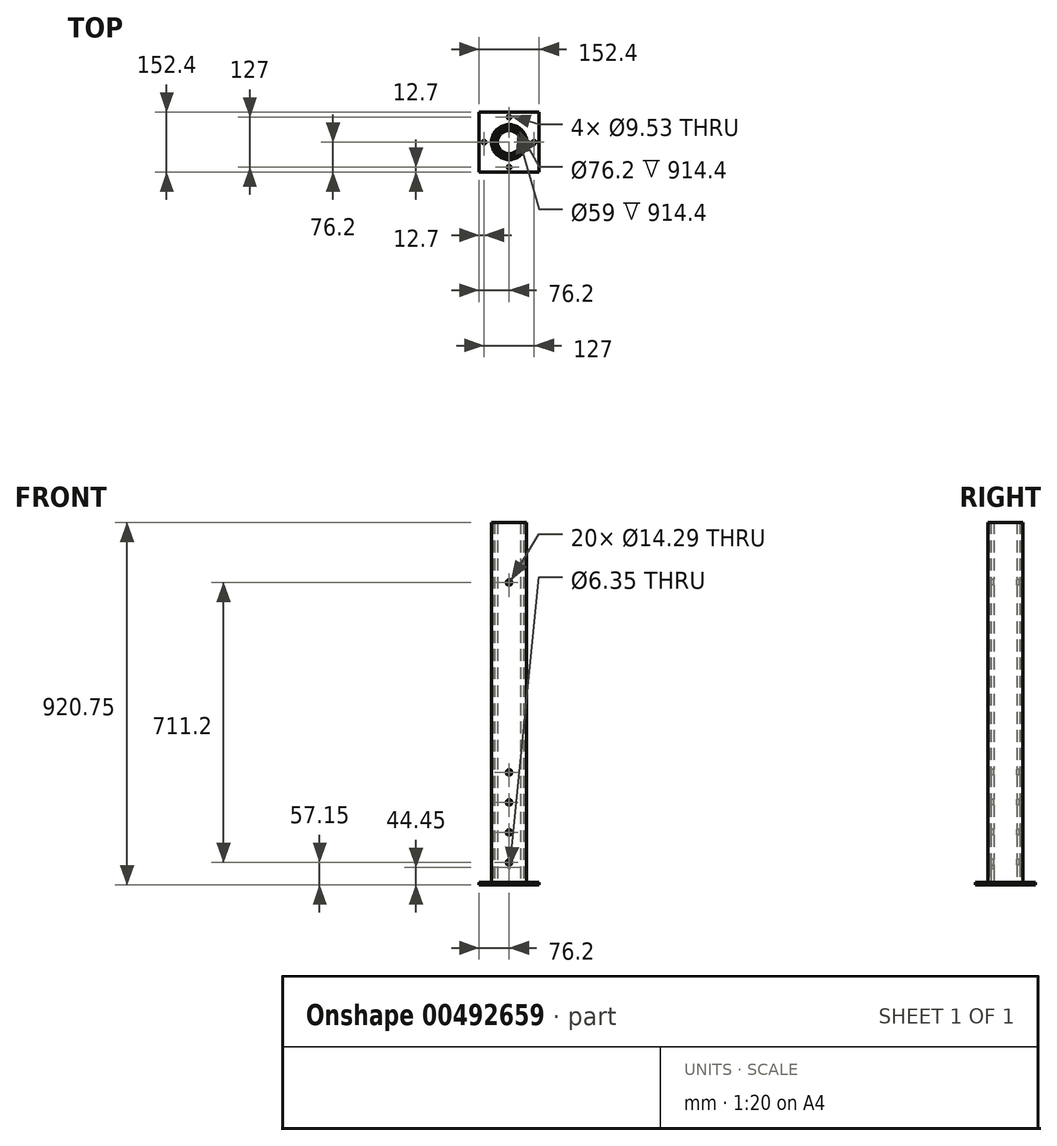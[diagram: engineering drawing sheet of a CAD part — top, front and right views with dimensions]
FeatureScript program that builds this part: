
annotation { "Feature Type Name" : "Feature", "Feature Type Description" : "" }
export const myFeature = defineFeature(function(context is Context, id is Id, definition is map)
    precondition{}
    {
        {
            var Q0;
            Q0=qCreatedBy(makeId("Top.planeOp"),FACE);
            var sketch = newSketch(context, id + "F0", { "sketchPlane" : qUnion([Q0])});
            skCircle(sketch, "E0", {"center": v(0, 0) * mm, "radius": 44.45 * mm});
            skCircle(sketch, "E1", {"center": v(0, 0) * mm, "radius": 38.1 * mm});
            skSolve(sketch);
        }
        {
            var Q0;
            Q0 = qSketchRegion(id + "F0", true);
            extrude(context, id + "F1", {"entities" : qUnion([Q0]), "depth" : 76.2 * mm, "offsetDistance" : 25 * mm});
        }
        {
            var Q0;
            Q0 = qSketchRegion(id + "F0", true);
            extrude(context, id + "F2", {"entities" : qUnion([Q0]), "depth" : 25.4 * mm, "offsetDistance" : 25 * mm});
        }
        {
            var Q0;
            Q0=qCreatedBy(makeId("Top.planeOp"),FACE);
            var sketch = newSketch(context, id + "F3", { "sketchPlane" : qUnion([Q0])});
            skCircle(sketch, "E2", {"center": v(0, 0) * mm, "radius": 36.51 * mm});
            skCircle(sketch, "E3", {"center": v(0, 0) * mm, "radius": 29.5 * mm});
            skSolve(sketch);
        }
        {
            var Q0;
            Q0 = qSketchRegion(id + "F3", true);
            extrude(context, id + "F4", {"entities" : qUnion([Q0]), "depth" : 914.4 * mm, "offsetDistance" : 25 * mm});
        }
        {
            var Q0;
            Q0=qCreatedBy(makeId("Front.planeOp"),FACE);
            var sketch = newSketch(context, id + "F5", { "sketchPlane" : qUnion([Q0])});
            skCircle(sketch, "E4", {"center": v(0, 38.1) * mm, "radius": 3.18 * mm});
            skSolve(sketch);
        }
        {
            var Q0;
            Q0 = qSketchRegion(id + "F5", true);
            extrude(context, id + "F6", {"entities" : qUnion([Q0]), "operationType" : NewBodyOperationType.REMOVE, "depth" : 50.8 * mm, "offsetDistance" : 25 * mm});
        }
        {
            var Q0;
            Q0=qCreatedBy(makeId("Top.planeOp"),FACE);
            var sketch = newSketch(context, id + "F7", { "sketchPlane" : qUnion([Q0])});
            skCircle(sketch, "E5", {"center": v(0, 0) * mm, "radius": 44.45 * mm});
            skCircle(sketch, "E6", {"center": v(0, 0) * mm, "radius": 38.1 * mm});
            skSolve(sketch);
        }
        {
            var Q0;
            Q0 = qSketchRegion(id + "F7", true);
            extrude(context, id + "F8", {"entities" : qUnion([Q0]), "depth" : 914.4 * mm, "offsetDistance" : 25 * mm});
        }
        {
            var Q0;
            Q0=qCreatedBy(makeId("Front.planeOp"),FACE);
            var sketch = newSketch(context, id + "F9", { "sketchPlane" : qUnion([Q0])});
            skCircle(sketch, "E7", {"center": v(0, 50.8) * mm, "radius": 7.14 * mm});
            skCircle(sketch, "E8.0.1.0", {"center": v(0, 127) * mm, "radius": 7.14 * mm});
            skCircle(sketch, "E8.0.2.0", {"center": v(0, 203.2) * mm, "radius": 7.14 * mm});
            skCircle(sketch, "E8.0.3.0", {"center": v(0, 279.4) * mm, "radius": 7.14 * mm});
            skLineSegment(sketch, "E8.direction1", {"start": v(0, 50.8) * mm, "end": v(25, 50.8) * mm, "construction": true});
            skLineSegment(sketch, "E8.direction2", {"start": v(0, 50.8) * mm, "end": v(0, 127) * mm, "construction": true});
            skSolve(sketch);
        }
        {
            var Q0;
            Q0 = qSketchRegion(id + "F9", true);
            extrude(context, id + "F10", {"entities" : qUnion([Q0]), "operationType" : NewBodyOperationType.REMOVE, "endBound" : BoundingType.THROUGH_ALL, "oppositeDirection" : true, "depth" : 25 * mm, "offsetDistance" : 25 * mm, "hasSecondDirection" : true, "secondDirectionBound" : BoundingType.THROUGH_ALL, "secondDirectionOppositeDirection" : false, "secondDirectionDepth" : 25 * mm});
        }
        {
            var Q0;
            Q0=qCreatedBy(makeId("Front.planeOp"),FACE);
            var sketch = newSketch(context, id + "F11", { "sketchPlane" : qUnion([Q0])});
            skCircle(sketch, "E9", {"center": v(0, 762) * mm, "radius": 7.14 * mm});
            skSolve(sketch);
        }
        {
            var Q0;
            Q0 = qSketchRegion(id + "F11", true);
            extrude(context, id + "F12", {"entities" : qUnion([Q0]), "operationType" : NewBodyOperationType.REMOVE, "endBound" : BoundingType.THROUGH_ALL, "oppositeDirection" : true, "depth" : 25 * mm, "offsetDistance" : 25 * mm, "hasSecondDirection" : true, "secondDirectionBound" : BoundingType.THROUGH_ALL, "secondDirectionOppositeDirection" : false, "secondDirectionDepth" : 25 * mm});
        }
        {
            var Q0;
            Q0=qCreatedBy(makeId("Top.planeOp"),FACE);
            var sketch = newSketch(context, id + "F13", { "sketchPlane" : qUnion([Q0])});
            skLineSegment(sketch, "E10.bottom", {"start": v(-76.2, -76.2) * mm, "end": v(76.2, -76.2) * mm});
            skLineSegment(sketch, "E10.top", {"start": v(-76.2, 76.2) * mm, "end": v(76.2, 76.2) * mm});
            skLineSegment(sketch, "E10.left", {"start": v(-76.2, -76.2) * mm, "end": v(-76.2, 76.2) * mm});
            skLineSegment(sketch, "E10.right", {"start": v(76.2, -76.2) * mm, "end": v(76.2, 76.2) * mm});
            skPoint(sketch, "E10.middle", {"position": v(0, 0) * mm});
            skCircle(sketch, "E11", {"center": v(63.5, 0) * mm, "radius": 4.76 * mm});
            skCircle(sketch, "E12.1.0", {"center": v(0, 63.5) * mm, "radius": 4.76 * mm});
            skCircle(sketch, "E12.2.0", {"center": v(-63.5, 0) * mm, "radius": 4.76 * mm});
            skCircle(sketch, "E12.3.0", {"center": v(0, -63.5) * mm, "radius": 4.76 * mm});
            skSolve(sketch);
        }
        {
            var Q0;
            Q0=makeQuery(id+"F13.imprint","IMPRINT",FACE,{"disambiguationData":[TD([[makeQuery(id+"F13.imprint","IMPRINT",EDGE,{"derivedFrom":sQuery(id+"F13.wireOp",EDGE,"E10.bottom")}),1.0]])]});
            extrude(context, id + "F14", {"entities" : qUnion([Q0]), "operationType" : NewBodyOperationType.ADD, "oppositeDirection" : true, "depth" : 6.35 * mm, "offsetDistance" : 25 * mm});
        }
    });
